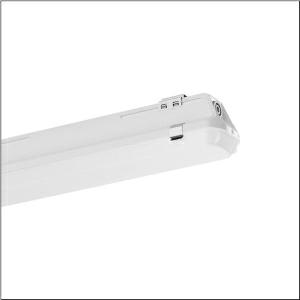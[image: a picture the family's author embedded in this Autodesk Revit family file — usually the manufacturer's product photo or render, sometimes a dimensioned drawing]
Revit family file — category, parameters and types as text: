
# Revit family: monsun_r__11_51fp208p430h_cbd4
name_source: partatom
category: Lighting Fixtures
units: mm (PartAtom-declared; Revit-internal decimal feet)

## family parameters
Cut with Voids When Loaded = No
Host = Face
Light Source = No
Part Type = Normal
Room Calculation Point = No
Round Connector Dimension = Use Diameter
Shared = No

## types (1)
- Monsun® 11 (1 x LED, 3990 lm, 24.8 W, 4000K)
    Apparent Load = 25 VA
    CIE Flux Codes = 45 75 93 94 100
    Color Rendering = 80
    Color Temperature = 4000K
    Default Elevation = 1800 mm
    Description = Monsun® 11, damp-proof luminaire, chain hanger, primary optical cover: enclosure, of PC, light emission: direct distribution, primary light characteristic: symmetric, installation type: suspended mounting, surface-mounted, horizontal mounting, vertical mounting, LED, rated luminous flux: 3.990lm, luminous efficacy: 161lm/W, light colour: 840, colour temperature: 4000K, control gear: ECG, with terminal, 3-pole, max. 2.5mm², mains connection: 220..240V, AC, 50/60Hz, rated input power: 25W, luminaire housing, of glass-fibre reinforced polyester, uncoated, bright grey, incl. chain hanger, length: 1.590mm, width: 90mm, height: 88mm, clip for enclosure, of stainless steel (V2A), ceiling mounting element, of stainless steel (V2A), chain hanger, of stainless steel (V2A), protection rating (complete): IP66, insulation class (complete): insulation class I (protective earthing), certification: CE, ENEC, VDE, UKCA, protection symbol: D, impact resistance: IK08, permissible operating ambient temperature: -35..+40°C, standard: EN 50419, EN 60598-2-1, no direct snow, no direct sun, no direct rain, for indoor or canopied outdoor use, corresponds to IFS (International Featured Standards) requirements for safety and quality in the food industry, contact your sales advisor before using the luminaires in applications with unclear chemical exposure, large temperature fluctuations or condensation-forming humidity, LABS conformity tested according to VDMA 24364:2018-05, packaging unit: 1 piece
    Height = 89 mm
    Lamp = 1 x LED
    Lamp Light Flux = 3990 lm
    Lamp Power = 24.8 W
    Lamp count = 1
    Length = 1590 mm
    Luminous efficacy = 161 lm/W
    Manufacturer = Siteco
    ModVariant = No
    Model = 51FP208P430H
    Mounting Place = Ceiling
    Mounting Type = Surface mounted
    Number of Poles = 1
    OnlyDefault = Yes
    Power Factor = 1
    Product Name = Monsun® 11
    Product group = damp-proof luminaire
    ProductGroupID = 301
    Protection Class = Protection class I
    Protection Degree = IP 66
    RLX_Detail_Level = 1
    RLX_Emergency_Light_Flux = 0 lm
    RLX_Emergency_Type = 0
    RLX_Emergency_Type_DB = No
    RlxData = <blob elided: 88809 chars, md5=5f140ee2>
    Socket = socket
    Standby Power = 0 W
    System Light Flux = 3990 lm
    System Power = 25 W
    Type Comments = Product without accessories
    Type Image = l_1004748.jpg
    URL = http://relux.com
    VarID = ---
    Voltage = 0 V
    Weight = 0.00 kg
    Width = 90 mm

## geometry (parser evidence)
native form markers: Blend x4, Sweep x14
no freeform markers — native parametric forms only
